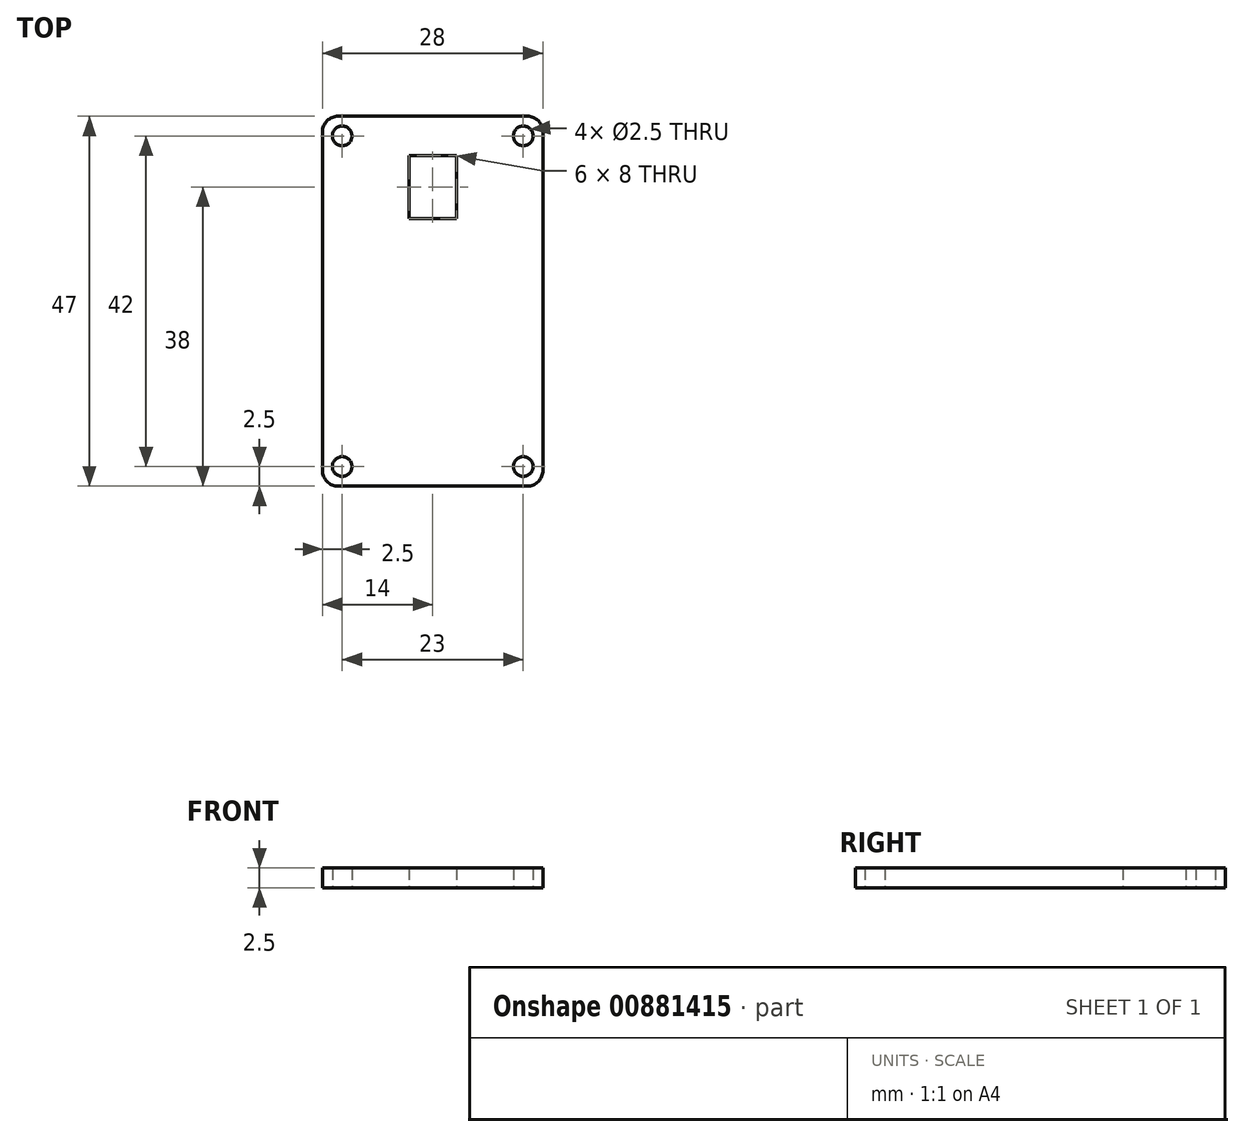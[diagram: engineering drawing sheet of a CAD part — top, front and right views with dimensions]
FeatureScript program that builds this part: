
annotation { "Feature Type Name" : "Feature", "Feature Type Description" : "" }
export const myFeature = defineFeature(function(context is Context, id is Id, definition is map)
    precondition{}
    {
        {
            var Q0;
            Q0=qCreatedBy(makeId("Top.planeOp"),FACE);
            var sketch = newSketch(context, id + "F0", { "sketchPlane" : qUnion([Q0])});
            skLineSegment(sketch, "E0.bottom", {"start": v(7.5, -16) * mm, "end": v(-10.5, -16) * mm});
            skLineSegment(sketch, "E0.top", {"start": v(7.5, 21) * mm, "end": v(-10.5, 21) * mm});
            skLineSegment(sketch, "E0.left", {"start": v(7.5, -16) * mm, "end": v(7.5, 21) * mm});
            skLineSegment(sketch, "E0.right", {"start": v(-10.5, -16) * mm, "end": v(-10.5, 21) * mm});
            skPoint(sketch, "E0.middle", {"position": v(-1.5, 2.5) * mm});
            skLineSegment(sketch, "E1.0", {"start": v(12.5, 26) * mm, "end": v(-15.5, 26) * mm});
            skLineSegment(sketch, "E1.1", {"start": v(12.5, -21) * mm, "end": v(12.5, 26) * mm});
            skLineSegment(sketch, "E1.2", {"start": v(12.5, -21) * mm, "end": v(-15.5, -21) * mm});
            skLineSegment(sketch, "E1.3", {"start": v(-15.5, -21) * mm, "end": v(-15.5, 26) * mm});
            skPoint(sketch, "E2", {"position": v(10, 23.5) * mm});
            skPoint(sketch, "E3", {"position": v(-13, 23.5) * mm});
            skPoint(sketch, "E4", {"position": v(-13, -18.5) * mm});
            skPoint(sketch, "E5", {"position": v(10, -18.5) * mm});
            skCircle(sketch, "E6", {"center": v(-13, -18.5) * mm, "radius": 1.25 * mm});
            skCircle(sketch, "E7", {"center": v(10, -18.5) * mm, "radius": 1.25 * mm});
            skCircle(sketch, "E8", {"center": v(10, 23.5) * mm, "radius": 1.25 * mm});
            skCircle(sketch, "E9", {"center": v(-13, 23.5) * mm, "radius": 1.25 * mm});
            skPoint(sketch, "E10", {"position": v(-4.5, 21) * mm});
            skPoint(sketch, "E11", {"position": v(1.5, 21) * mm});
            skPoint(sketch, "E12", {"position": v(1.5, 13) * mm});
            skPoint(sketch, "E13", {"position": v(-4.5, 13) * mm});
            skLineSegment(sketch, "E14", {"start": v(-4.5, 21) * mm, "end": v(-4.5, 13) * mm});
            skLineSegment(sketch, "E15", {"start": v(-4.5, 13) * mm, "end": v(1.5, 13) * mm});
            skLineSegment(sketch, "E16", {"start": v(1.5, 13) * mm, "end": v(1.5, 21) * mm});
            skSolve(sketch);
        }
        {
            var Q0;
            {var subQ4=sQuery(id+"F0.wireOp",EDGE,"E0.bottom");Q0=makeQuery(id+"F0.imprint","IMPRINT",FACE,{"disambiguationData":[TD([[makeQuery(id+"F0.imprint","IMPRINT",EDGE,{"derivedFrom":subQ4}),1.0]])]});}
            var Q1;
            {var subQ1=sQuery(id+"F0.wireOp",EDGE,"E0.bottom");Q1=makeQuery(id+"F0.imprint","IMPRINT",FACE,{"disambiguationData":[TD([[makeQuery(id+"F0.imprint","IMPRINT",EDGE,{"derivedFrom":subQ1}),-1.0]])]});}
            extrude(context, id + "F1", {"entities" : qUnion([Q0, Q1]), "depth" : 2.5 * mm, "offsetDistance" : 25 * mm});
        }
        {
            var Q0;
            Q0=makeQuery(id+"F1.opExtrude","SWEPT_EDGE",EDGE,{"disambiguationData":[OSD([sQuery(id+"F0.wireOp",EDGE,"E1.0"),sQuery(id+"F0.wireOp",EDGE,"E1.3")])]});
            var Q1;
            Q1=makeQuery(id+"F1.opExtrude","SWEPT_EDGE",EDGE,{"disambiguationData":[OSD([sQuery(id+"F0.wireOp",EDGE,"E1.0"),sQuery(id+"F0.wireOp",EDGE,"E1.1")])]});
            var Q2;
            Q2=makeQuery(id+"F1.opExtrude","SWEPT_EDGE",EDGE,{"disambiguationData":[OSD([sQuery(id+"F0.wireOp",EDGE,"E1.1"),sQuery(id+"F0.wireOp",EDGE,"E1.2")])]});
            var Q3;
            Q3=makeQuery(id+"F1.opExtrude","SWEPT_EDGE",EDGE,{"disambiguationData":[OSD([sQuery(id+"F0.wireOp",EDGE,"E1.2"),sQuery(id+"F0.wireOp",EDGE,"E1.3")])]});
            fillet(context, id + "F2", {"entities" : qUnion([Q0, Q1, Q2, Q3]), "tangentPropagation" : true, "radius" : 2 * mm, "defaultsChanged" : true, "vertexSettings" : [], "allowEdgeOverflow" : false});
        }
    });
